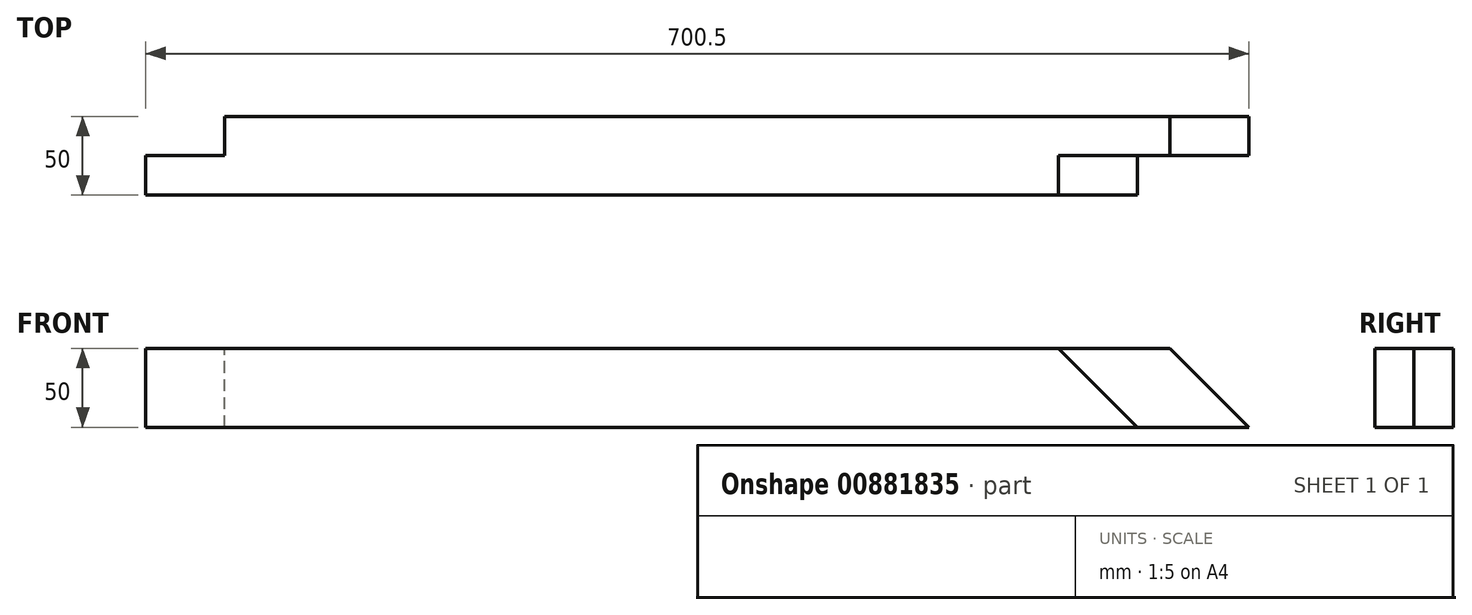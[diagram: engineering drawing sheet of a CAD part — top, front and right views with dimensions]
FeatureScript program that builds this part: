
annotation { "Feature Type Name" : "Feature", "Feature Type Description" : "" }
export const myFeature = defineFeature(function(context is Context, id is Id, definition is map)
    precondition{}
    {
        {
            var Q0;
            Q0=qCreatedBy(makeId("Front.planeOp"),FACE);
            var sketch = newSketch(context, id + "F0", { "sketchPlane" : qUnion([Q0])});
            skLineSegment(sketch, "E0", {"start": v(874.1, 24.7) * mm, "end": v(1574.6, 24.7) * mm});
            skLineSegment(sketch, "E1", {"start": v(1524.6, 74.7) * mm, "end": v(874.1, 74.7) * mm});
            skLineSegment(sketch, "E2", {"start": v(874.1, 74.7) * mm, "end": v(874.1, 24.7) * mm});
            skLineSegment(sketch, "E3", {"start": v(1574.6, 24.7) * mm, "end": v(1524.6, 74.7) * mm});
            skSolve(sketch);
        }
        {
            var Q0;
            Q0=qSketchRegion(id+"F0",true);
            extrude(context, id + "F1", {"entities" : qUnion([Q0]), "depth" : 50 * mm, "offsetDistance" : 25 * mm});
        }
        {
            var Q0;
            Q0=makeQuery(id+"F1.opExtrude","CAP_FACE",FACE,{"disambiguationData":[OSD([sQuery(id+"F0.wireOp",EDGE,"E0"),sQuery(id+"F0.wireOp",EDGE,"E1"),sQuery(id+"F0.wireOp",EDGE,"E2"),sQuery(id+"F0.wireOp",EDGE,"E3")])],"isStart":false});
            var sketch = newSketch(context, id + "F2", { "sketchPlane" : qUnion([Q0])});
            skLineSegment(sketch, "E4", {"start": v(1574.6, 24.7) * mm, "end": v(1524.6, 74.7) * mm});
            skLineSegment(sketch, "E5", {"start": v(1453.89, 74.7) * mm, "end": v(1503.89, 24.7) * mm});
            skLineSegment(sketch, "E6", {"start": v(1524.6, 74.7) * mm, "end": v(1453.89, 74.7) * mm});
            skLineSegment(sketch, "E7", {"start": v(1574.6, 24.7) * mm, "end": v(1503.89, 24.7) * mm});
            skSolve(sketch);
        }
        {
            var Q0;
            Q0=qSketchRegion(id+"F2",true);
            extrude(context, id + "F3", {"entities" : qUnion([Q0]), "operationType" : NewBodyOperationType.REMOVE, "oppositeDirection" : true, "depth" : 25 * mm, "offsetDistance" : 25 * mm});
        }
        {
            var Q0;
            Q0=makeQuery(id+"F1.opExtrude","CAP_FACE",FACE,{"disambiguationData":[OSD([sQuery(id+"F0.wireOp",EDGE,"E0"),sQuery(id+"F0.wireOp",EDGE,"E1"),sQuery(id+"F0.wireOp",EDGE,"E2"),sQuery(id+"F0.wireOp",EDGE,"E3")])],"isStart":true});
            var sketch = newSketch(context, id + "F4", { "sketchPlane" : qUnion([Q0])});
            skLineSegment(sketch, "E8.bottom", {"start": v(-874.1, 24.7) * mm, "end": v(-924.1, 24.7) * mm});
            skLineSegment(sketch, "E8.top", {"start": v(-874.1, 74.7) * mm, "end": v(-924.1, 74.7) * mm});
            skLineSegment(sketch, "E8.left", {"start": v(-874.1, 24.7) * mm, "end": v(-874.1, 74.7) * mm});
            skLineSegment(sketch, "E8.right", {"start": v(-924.1, 24.7) * mm, "end": v(-924.1, 74.7) * mm});
            skSolve(sketch);
        }
        {
            var Q0;
            Q0=qSketchRegion(id+"F4",true);
            extrude(context, id + "F5", {"entities" : qUnion([Q0]), "operationType" : NewBodyOperationType.REMOVE, "oppositeDirection" : true, "depth" : 25 * mm, "offsetDistance" : 25 * mm});
        }
    });
